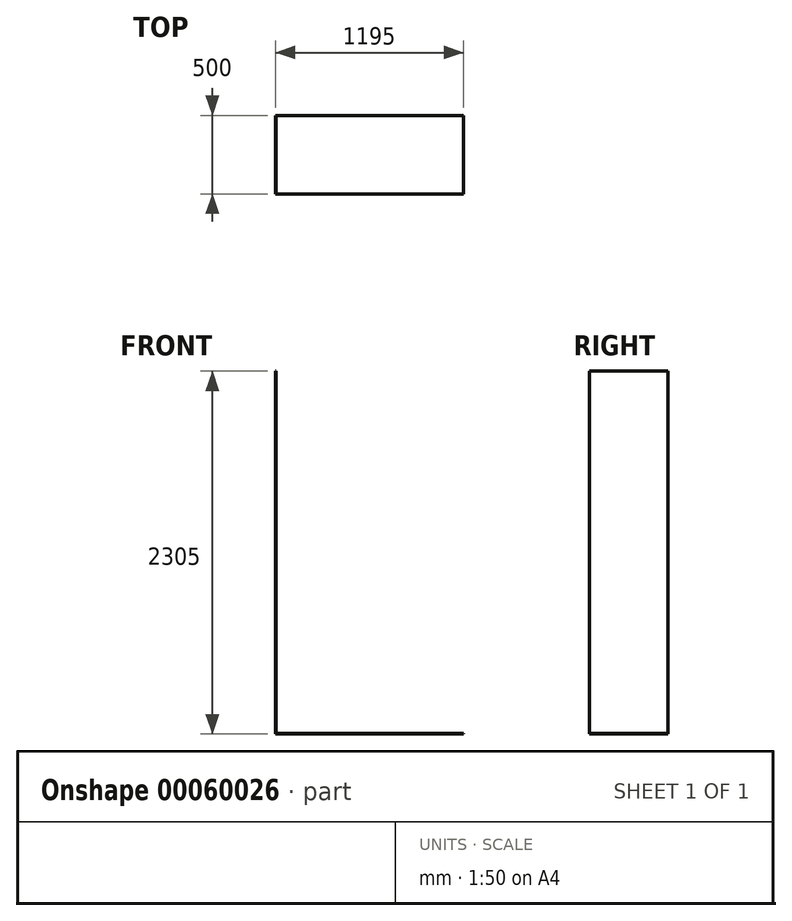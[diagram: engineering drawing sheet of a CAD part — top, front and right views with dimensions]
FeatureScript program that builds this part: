
annotation { "Feature Type Name" : "Feature", "Feature Type Description" : "" }
export const myFeature = defineFeature(function(context is Context, id is Id, definition is map)
    precondition{}
    {
        {
            var Q0;
            Q0=qCreatedBy(makeId("Top.planeOp"),FACE);
            var sketch = newSketch(context, id + "F0", { "sketchPlane" : qUnion([Q0])});
            skLineSegment(sketch, "E0.bottom", {"start": v(595, 250) * mm, "end": v(-595, 250) * mm});
            skLineSegment(sketch, "E0.top", {"start": v(595, -250) * mm, "end": v(-595, -250) * mm});
            skLineSegment(sketch, "E0.left", {"start": v(595, 250) * mm, "end": v(595, -250) * mm});
            skLineSegment(sketch, "E0.right", {"start": v(-595, 250) * mm, "end": v(-595, -250) * mm});
            skPoint(sketch, "E0.middle", {"position": v(0, 0) * mm});
            skSolve(sketch);
        }
        {
            var Q0;
            Q0=makeQuery(id+"F0.imprint","IMPRINT",FACE,{"disambiguationData":[TD([[makeQuery(id+"F0.imprint","IMPRINT",EDGE,{"derivedFrom":sQuery(id+"F0.wireOp",EDGE,"E0.bottom")}),1.0]])]});
            extrude(context, id + "F1", {"entities" : qUnion([Q0]), "oppositeDirection" : true, "depth" : 5 * mm});
        }
        {
            var Q0;
            Q0=makeQuery(id+"F1.opExtrude","SWEPT_FACE",FACE,{"disambiguationData":[OSD([sQuery(id+"F0.wireOp",EDGE,"E0.right")])]});
            var sketch = newSketch(context, id + "F2", { "sketchPlane" : qUnion([Q0])});
            skLineSegment(sketch, "E1.bottom", {"start": v(-250, 0) * mm, "end": v(250, 0) * mm});
            skLineSegment(sketch, "E1.top", {"start": v(-250, 2300) * mm, "end": v(250, 2300) * mm});
            skLineSegment(sketch, "E1.left", {"start": v(-250, 0) * mm, "end": v(-250, 2300) * mm});
            skLineSegment(sketch, "E1.right", {"start": v(250, 0) * mm, "end": v(250, 2300) * mm});
            skSolve(sketch);
        }
        {
            var Q0;
            Q0=makeQuery(id+"F2.imprint","IMPRINT",FACE,{"disambiguationData":[TD([[makeQuery(id+"F2.imprint","IMPRINT",EDGE,{"derivedFrom":sQuery(id+"F2.wireOp",EDGE,"E1.bottom")}),-1.0]])]});
            var Q1;
            Q1=makeQuery(id+"F2.imprint","IMPRINT",FACE,{"disambiguationData":[TD([[makeQuery(id+"F2.imprint","IMPRINT",EDGE,{"derivedFrom":sQuery(id+"F2.wireOp",EDGE,"E1.bottom")}),1.0]])]});
            extrude(context, id + "F3", {"entities" : qUnion([Q0, Q1]), "operationType" : NewBodyOperationType.ADD, "depth" : 5 * mm});
        }
        {
            var Q0;
            Q0=makeQuery(id+"F0.imprint","IMPRINT",FACE,{"disambiguationData":[TD([[makeQuery(id+"F0.imprint","IMPRINT",EDGE,{"derivedFrom":sQuery(id+"F0.wireOp",EDGE,"E0.bottom")}),1.0]])]});
            var Q1;
            Q1=sQuery(id+"F0.wireOp",EDGE,"E0.bottom");
            var Q2;
            Q2=sQuery(id+"F0.wireOp",EDGE,"E0.right");
            var Q3;
            Q3=sQuery(id+"F0.wireOp",EDGE,"E0.top");
            var Q4;
            Q4=sQuery(id+"F0.wireOp",EDGE,"E0.left");
            extrude(context, id + "F4", {"entities" : qUnion([Q0]), "bodyType" : ToolBodyType.SURFACE, "surfaceEntities" : qUnion([Q1, Q2, Q3, Q4]), "depth" : 5 * mm});
        }
    });
